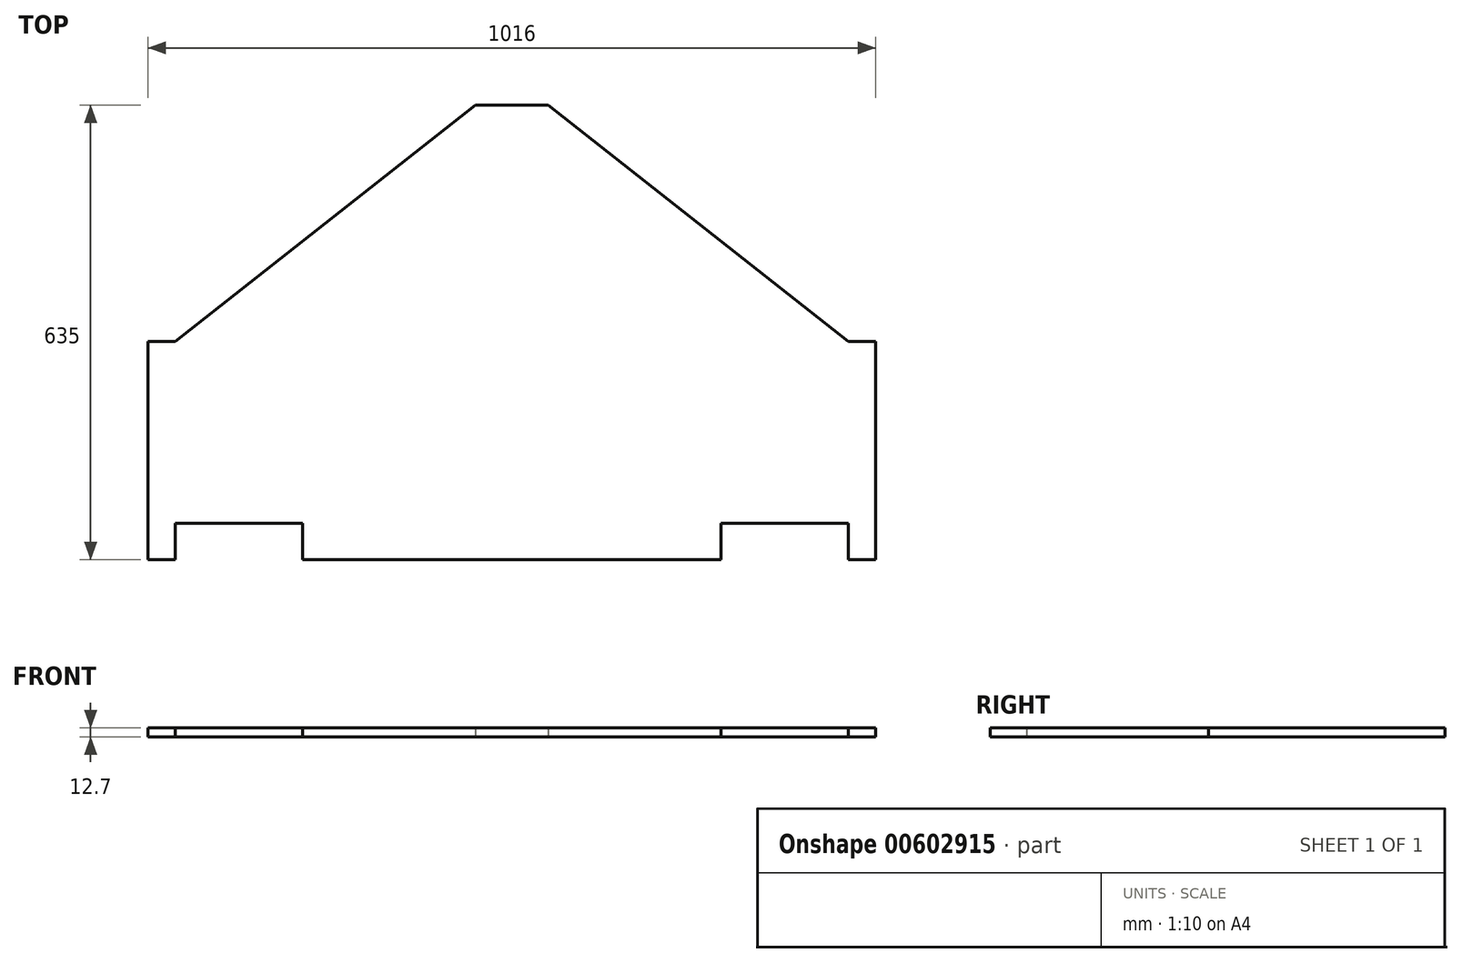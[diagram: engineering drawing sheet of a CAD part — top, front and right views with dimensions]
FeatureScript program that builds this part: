
annotation { "Feature Type Name" : "Feature", "Feature Type Description" : "" }
export const myFeature = defineFeature(function(context is Context, id is Id, definition is map)
    precondition{}
    {
        {
            var Q0;
            Q0=qCreatedBy(makeId("Top.planeOp"),FACE);
            var sketch = newSketch(context, id + "F0", { "sketchPlane" : qUnion([Q0])});
            skLineSegment(sketch, "E0", {"start": v(-506.26, -50.8) * mm, "end": v(-506.26, 254) * mm});
            skLineSegment(sketch, "E1", {"start": v(-506.26, -50.8) * mm, "end": v(-468.16, -50.8) * mm});
            skLineSegment(sketch, "E2", {"start": v(-468.16, -50.8) * mm, "end": v(-468.16, 0) * mm});
            skLineSegment(sketch, "E3", {"start": v(-468.16, 0) * mm, "end": v(-290.36, 0) * mm});
            skLineSegment(sketch, "E4", {"start": v(-290.36, 0) * mm, "end": v(-290.36, -50.8) * mm});
            skLineSegment(sketch, "E5", {"start": v(-290.36, -50.8) * mm, "end": v(293.84, -50.8) * mm});
            skLineSegment(sketch, "E6", {"start": v(293.84, -50.8) * mm, "end": v(293.84, 0) * mm});
            skLineSegment(sketch, "E7", {"start": v(293.84, 0) * mm, "end": v(471.64, 0) * mm});
            skLineSegment(sketch, "E8", {"start": v(471.64, 0) * mm, "end": v(471.64, -50.8) * mm});
            skLineSegment(sketch, "E9", {"start": v(471.64, -50.8) * mm, "end": v(509.74, -50.8) * mm});
            skLineSegment(sketch, "E10", {"start": v(509.74, -50.8) * mm, "end": v(509.74, 254) * mm});
            skLineSegment(sketch, "E11", {"start": v(-506.26, 254) * mm, "end": v(-468.16, 254) * mm});
            skLineSegment(sketch, "E12", {"start": v(509.74, 254) * mm, "end": v(471.64, 254) * mm});
            skLineSegment(sketch, "E13", {"start": v(-468.16, 254) * mm, "end": v(-49.06, 584.2) * mm});
            skLineSegment(sketch, "E14", {"start": v(-49.06, 584.2) * mm, "end": v(52.54, 584.2) * mm});
            skLineSegment(sketch, "E15", {"start": v(52.54, 584.2) * mm, "end": v(471.64, 254) * mm});
            skSolve(sketch);
        }
        {
            var Q0;
            Q0 = qSketchRegion(id + "F0", true);
            extrude(context, id + "F1", {"entities" : qUnion([Q0]), "depth" : 12.7 * mm, "offsetDistance" : 25.4 * mm});
        }
    });
